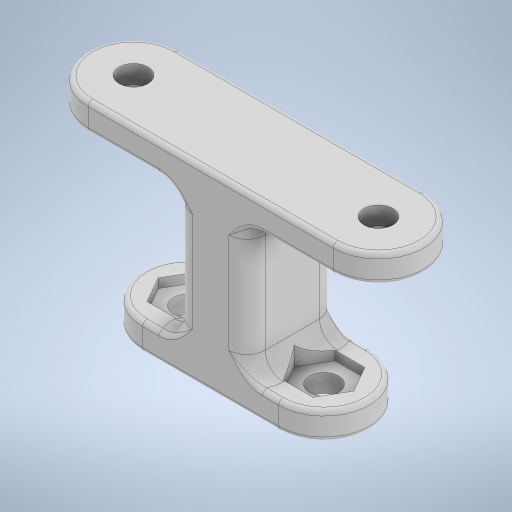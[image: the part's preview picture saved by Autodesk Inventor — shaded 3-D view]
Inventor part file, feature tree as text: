
AUTODESK INVENTOR PART (.ipt)
format: ipt  version: 2024.2 (Build 282272000, 272)  size: 432,640 bytes
history: native  units: mm
features: extrude x6, sketch x6, fillet x2
ambient origin geometry x8: Origin, YZ Plane, XZ Plane, XY Plane, X Axis, Y Axis, Z Axis, Center Point
bodies: Solid1 (feature_tree)
feature tree (14):
  extrude  "Extrusion1"  Depth=27.0mm
  extrude  "Extrusion2"  Depth=10.0mm TaperAngle=0.0deg
  extrude  "Extrusion3"  Depth=15.0mm
  extrude  "Extrusion4"  Depth=5.7mm
  extrude  "Extrusion5"  Depth=3.2mm
  extrude  "Extrusion6"  Depth=0.5mm
  fillet  "Fillet3"  Radius=1.0mm
  fillet  "Fillet2"  Radius=0.5mm
  sketch  "Sketch1"  dims[d0=3.2mm d1=27.0mm]
  sketch  "Sketch2"  dims[d2=10.0mm d3=3.0mm d4=0.0mm]
  sketch  "Sketch3"  dims[d5=15.0mm d6=0.0mm d7=15.0mm]
  sketch  "Sketch4"  dims[d8=3.0mm d9=0.0mm d10=5.7mm]
  sketch  "Sketch5"  dims[d11=1.0mm d12=0.0mm d13=3.2mm]
  sketch  "Sketch6"  dims[d14=2.0mm d15=0.0mm d16=5.1mm d17=1.0mm d18=0.0mm d20=0.5mm d22=8.0mm d23=2.0mm]
